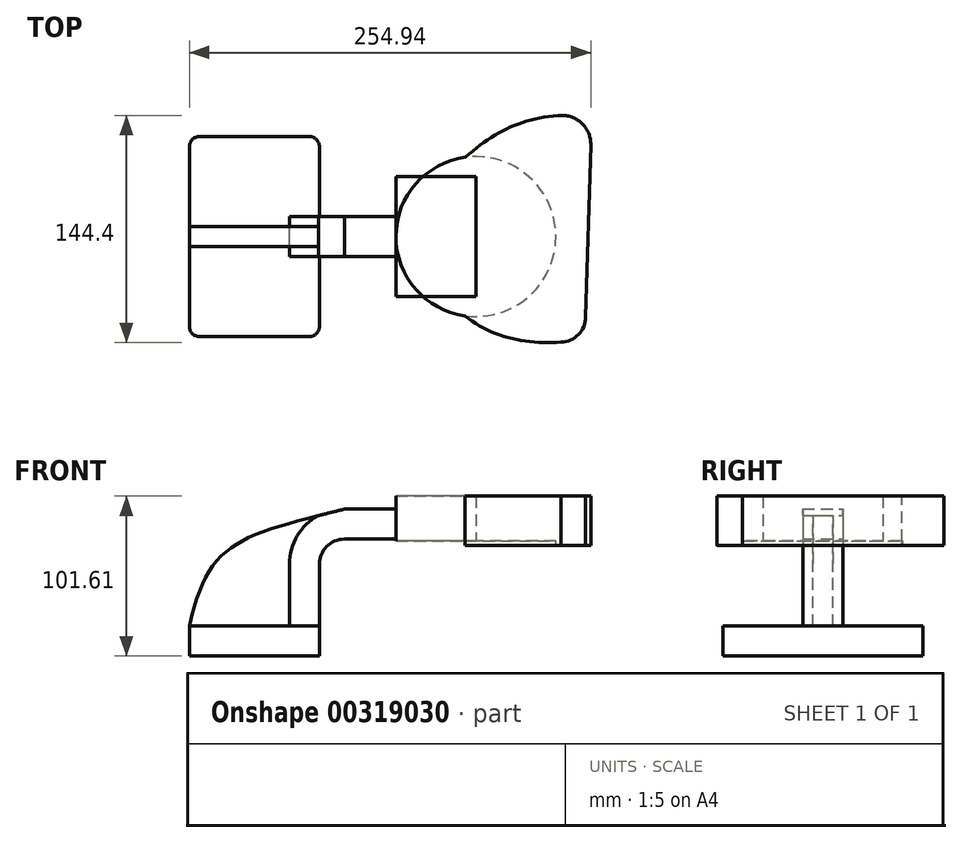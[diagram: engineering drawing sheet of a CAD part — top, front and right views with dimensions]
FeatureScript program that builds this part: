
annotation { "Feature Type Name" : "Feature", "Feature Type Description" : "" }
export const myFeature = defineFeature(function(context is Context, id is Id, definition is map)
    precondition{}
    {
        {
            var Q0;
            Q0=qCreatedBy(makeId("Front.planeOp"),FACE);
            var sketch = newSketch(context, id + "F0", { "sketchPlane" : qUnion([Q0])});
            skLineSegment(sketch, "E0.bottom", {"start": v(-41.28, 9.52) * mm, "end": v(41.27, 9.53) * mm});
            skLineSegment(sketch, "E0.top", {"start": v(-41.28, -9.53) * mm, "end": v(41.28, -9.53) * mm});
            skLineSegment(sketch, "E0.left", {"start": v(-41.28, 9.52) * mm, "end": v(-41.28, -9.53) * mm});
            skLineSegment(sketch, "E0.right", {"start": v(41.27, 9.53) * mm, "end": v(41.28, -9.52) * mm});
            skPoint(sketch, "E0.middle", {"position": v(0, 0) * mm});
            skLineSegment(sketch, "E1.bottom", {"start": v(140.7, 92.08) * mm, "end": v(89.9, 92.08) * mm});
            skLineSegment(sketch, "E1.top", {"start": v(140.7, 63.5) * mm, "end": v(89.9, 63.5) * mm});
            skLineSegment(sketch, "E1.left", {"start": v(140.7, 92.08) * mm, "end": v(140.7, 63.5) * mm});
            skLineSegment(sketch, "E1.right", {"start": v(89.9, 92.08) * mm, "end": v(89.9, 63.5) * mm});
            skPoint(sketch, "E1.middle", {"position": v(115.3, 77.79) * mm});
            skLineSegment(sketch, "E2", {"start": v(41.27, 9.53) * mm, "end": v(41.27, 48.93) * mm});
            skArc(sketch, "E3", {"start": v(41.27, 48.93) * mm, "mid": v(45.92, 60.16) * mm, "end": v(57.15, 64.8) * mm});
            skLineSegment(sketch, "E4", {"start": v(57.15, 64.8) * mm, "end": v(102.3, 64.8) * mm});
            skLineSegment(sketch, "E5.0", {"start": v(57.15, 83.86) * mm, "end": v(102.3, 83.86) * mm});
            skArc(sketch, "E5.1", {"start": v(22.23, 48.93) * mm, "mid": v(32.45, 73.63) * mm, "end": v(57.15, 83.86) * mm});
            skLineSegment(sketch, "E5.2", {"start": v(22.22, 9.53) * mm, "end": v(22.22, 48.93) * mm});
            skFitSpline(sketch, "E6", {"points": [v(-41.28, 9.52) * mm, v(57.15, 83.86) * mm], "startDerivative": vector(35.5, 162.28) * mm, "endDerivative": vector(201.47, 50.62) * mm});
            skSolve(sketch);
        }
        {
            var Q0;
            Q0=makeQuery(id+"F0.imprint","IMPRINT",FACE,{"disambiguationData":[TD([[makeQuery(id+"F0.imprint","IMPRINT",EDGE,{"derivedFrom":sQuery(id+"F0.wireOp",EDGE,"E0.top")}),1.0]])]});
            extrude(context, id + "F1", {"entities" : qUnion([Q0]), "endBound" : BoundingType.SYMMETRIC, "depth" : 127 * mm, "hasSecondDirection" : true, "secondDirectionOppositeDirection" : true, "secondDirectionDepth" : 50.04 * mm});
        }
        {
            var Q0;
            {var subQ1=sQuery(id+"F0.wireOp",EDGE,"E2");Q0=makeQuery(id+"F0.imprint","IMPRINT",FACE,{"disambiguationData":[TD([[makeQuery(id+"F0.imprint","IMPRINT",EDGE,{"derivedFrom":subQ1}),1.0]])]});}
            extrude(context, id + "F2", {"entities" : qUnion([Q0]), "endBound" : BoundingType.SYMMETRIC, "depth" : 25.4 * mm});
        }
        {
            var Q0;
            {var subQ1=sQuery(id+"F0.wireOp",EDGE,"E1.bottom");Q0=makeQuery(id+"F0.imprint","IMPRINT",FACE,{"disambiguationData":[TD([[makeQuery(id+"F0.imprint","IMPRINT",EDGE,{"derivedFrom":subQ1}),1.0]])]});}
            extrude(context, id + "F3", {"entities" : qUnion([Q0]), "operationType" : NewBodyOperationType.ADD, "endBound" : BoundingType.SYMMETRIC, "depth" : 76.2 * mm});
        }
        {
            var Q0;
            {var subQ3=sQuery(id+"F0.wireOp",EDGE,"E5.2");Q0=makeQuery(id+"F0.imprint","IMPRINT",FACE,{"disambiguationData":[TD([[makeQuery(id+"F0.imprint","IMPRINT",EDGE,{"derivedFrom":subQ3}),1.0]])]});}
            extrude(context, id + "F4", {"entities" : qUnion([Q0]), "endBound" : BoundingType.SYMMETRIC, "depth" : 12.7 * mm});
        }
        {
            var Q0;
            {var subQ1=sQuery(id+"F0.wireOp",EDGE,"E1.bottom");Q0=makeQuery(id+"F0.imprint","IMPRINT",FACE,{"disambiguationData":[TD([[makeQuery(id+"F0.imprint","IMPRINT",EDGE,{"derivedFrom":subQ1}),1.0]])]});}
            var Q1;
            Q1=sQuery(id+"F0.wireOp",EDGE,"E1.left");
            revolve(context, id + "F5", {"entities" : qUnion([Q0]), "axis" : qUnion([Q1]), "revolveType" : RevolveType.FULL});
        }
        {
            var Q0;
            Q0=makeQuery(id+"F5.opRevolve","SWEPT_FACE",FACE,{"disambiguationData":[OSD([sQuery(id+"F0.wireOp",EDGE,"E1.bottom")])]});
            var sketch = newSketch(context, id + "F6", { "sketchPlane" : qUnion([Q0])});
            skCircle(sketch, "E7", {"center": v(195.38, 58.71) * mm, "radius": 18.28 * mm});
            skCircle(sketch, "E8", {"center": v(194.33, -51) * mm, "radius": 16.13 * mm});
            skLineSegment(sketch, "E9", {"start": v(210.46, -51) * mm, "end": v(213.66, 58.18) * mm});
            skFitSpline(sketch, "E10", {"points": [v(195.4, 77) * mm, v(134.13, 50.37) * mm], "startDerivative": vector(-74.93, -4.15) * mm, "endDerivative": vector(-54.6, -49.68) * mm});
            skFitSpline(sketch, "E11", {"points": [v(194.68, -67.12) * mm, v(133.83, -50.33) * mm], "startDerivative": vector(-63.87, -4.54) * mm, "endDerivative": vector(-50.54, 41.78) * mm});
            skSolve(sketch);
        }
        {
            var Q0;
            {var subQ0=sQuery(id+"F6.wireOp",EDGE,"E10");var subQ1=sQuery(id+"F6.wireOp",EDGE,"E7");var subQ2=makeQuery(id+"F6.imprint","INTERSECT",VERTEX,{"disambiguationData":[OD(0.0)],"derivedFrom":[subQ1,subQ0]});Q0=makeQuery(id+"F6.imprint","IMPRINT",FACE,{"disambiguationData":[TD([[makeQuery(id+"F6.imprint","IMPRINT",EDGE,{"disambiguationData":[TD([[subQ2,-1.0]])],"derivedFrom":subQ1}),1.0]])]});}
            var Q1;
            {var subQ5=sQuery(id+"F6.wireOp",EDGE,"E9");Q1=makeQuery(id+"F6.imprint","IMPRINT",FACE,{"disambiguationData":[TD([[makeQuery(id+"F6.imprint","IMPRINT",EDGE,{"derivedFrom":subQ5}),1.0]])]});}
            var Q2;
            {var subQ0=sQuery(id+"F6.wireOp",EDGE,"E7");var subQ1=makeQuery(id+"F6.imprint","INTERSECT",VERTEX,{"derivedFrom":[subQ0,sQuery(id+"F6.wireOp",EDGE,"E9")]});Q2=makeQuery(id+"F6.imprint","IMPRINT",FACE,{"disambiguationData":[TD([[makeQuery(id+"F6.imprint","IMPRINT",EDGE,{"disambiguationData":[TD([[subQ1,1.0]])],"derivedFrom":subQ0}),1.0]])]});}
            var Q3;
            {var subQ0=sQuery(id+"F6.wireOp",EDGE,"E8");var subQ1=makeQuery(id+"F6.imprint","INTERSECT",VERTEX,{"derivedFrom":[subQ0,sQuery(id+"F6.wireOp",EDGE,"E9")]});Q3=makeQuery(id+"F6.imprint","IMPRINT",FACE,{"disambiguationData":[TD([[makeQuery(id+"F6.imprint","IMPRINT",EDGE,{"disambiguationData":[TD([[subQ1,-1.0]])],"derivedFrom":subQ0}),1.0]])]});}
            extrude(context, id + "F7", {"entities" : qUnion([Q0, Q1, Q2, Q3]), "operationType" : NewBodyOperationType.ADD, "oppositeDirection" : true, "depth" : 31.24 * mm});
        }
        {
            var Q0;
            Q0=makeQuery(id+"F1.opExtrude","CAP_EDGE",EDGE,{"disambiguationData":[OSD([sQuery(id+"F0.wireOp",EDGE,"E0.left")])],"isStart":false});
            var Q1;
            Q1=makeQuery(id+"F1.opExtrude","CAP_EDGE",EDGE,{"disambiguationData":[OSD([sQuery(id+"F0.wireOp",EDGE,"E0.left")])],"isStart":true});
            var Q2;
            Q2=makeQuery(id+"F1.opExtrude","CAP_EDGE",EDGE,{"disambiguationData":[OSD([sQuery(id+"F0.wireOp",EDGE,"E0.right")])],"isStart":true});
            var Q3;
            Q3=makeQuery(id+"F1.opExtrude","CAP_EDGE",EDGE,{"disambiguationData":[OSD([sQuery(id+"F0.wireOp",EDGE,"E0.right")])],"isStart":false});
            fillet(context, id + "F8", {"entities" : qUnion([Q0, Q1, Q2, Q3]), "radius" : 6.35 * mm, "tangentPropagation" : true, "allowEdgeOverflow" : false});
        }
    });
